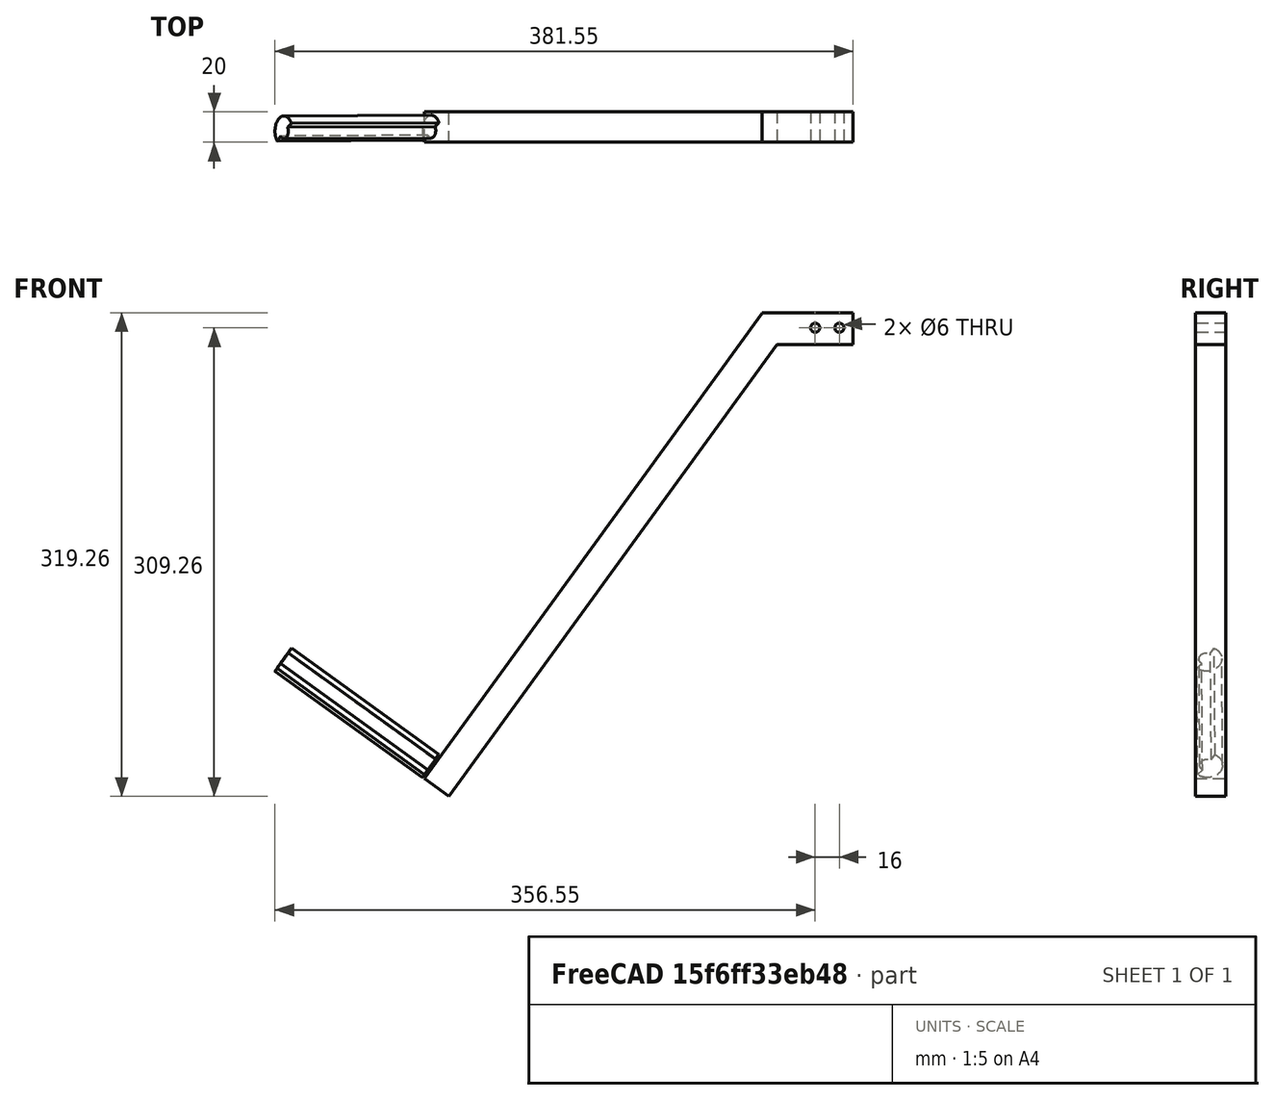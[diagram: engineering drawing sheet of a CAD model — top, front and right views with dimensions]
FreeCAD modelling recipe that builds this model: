
FCSTD DOCUMENT  (FreeCAD 0.16R6704 (Git))
Label: soporte reposapies derecho
License: All rights reserved
LicenseURL: http://en.wikipedia.org/wiki/All_rights_reserved
objects: Part::Cylinder×7, Part::Cut×6, Part::Box×2, Part::MultiFuse×2
note: 17 computed .brp shape members not serialized (recipe doc carries the construction recipe); baked Part::Feature solids carry a one-line shape summary decoded from their .brp

FEATURE [Part::Cylinder] Cylinder194  label="Agujero reposapies003"
  Angle = 360
  Height = 50
  Placement = pos=(-466,485,211) rot=(1,0,0;1.5708rad)
  Radius = 3
FEATURE [Part::Box] Box127  label="Cubo090"
  Height = 380
  Length = 20
  Placement = pos=(-291,469,-86.5) rot=(0,1,0;0.628319rad)
  Width = 20
FEATURE [Part::Box] Box128  label="Cubo091"
  Height = 21
  Length = 60
  Placement = pos=(-68,469,200) rot=(0,0,1;0rad)
  Width = 20
FEATURE [Part::MultiFuse] Fusion077
  Placement = pos=(15,0,0) rot=(0,0,1;0rad)
  Shapes = -> [Box127,Box128]
FEATURE [Part::Cylinder] Cylinder264  label="Cilindro154"
  Angle = 360
  Height = 37
  Placement = pos=(-2,496,211) rot=(1,0,0;1.5708rad)
  Radius = 3
FEATURE [Part::Cut] Cut283
  Base = -> Fusion077
  Placement = pos=(-448,-19,0) rot=(0,0,1;0rad)
  Tool = -> Cylinder264
FEATURE [Part::Cut] Cut286
  Base = -> Cut283
  Tool = -> Cylinder194
FEATURE [Part::Cylinder] Cylinder268  label="Cilindro155"
  Angle = 360
  Height = 120
  Placement = pos=(-292,0,98.9) rot=(0,1,0;2.19911rad)
  Radius = 10
FEATURE [Part::Cylinder] Cylinder269  label="Cilindro156"
  Angle = 50
  Height = 130
  Placement = pos=(-292,0,98.9) rot=(0,1,0;2.19911rad)
  Radius = 11
FEATURE [Part::Cylinder] Cylinder270  label="Cilindro157"
  Angle = 360
  Height = 130
  Placement = pos=(-292,0,98.9) rot=(0,1,0;2.19911rad)
  Radius = 5
FEATURE [Part::Cut] Cut289
  Base = -> Cylinder269
  Tool = -> Cylinder270
FEATURE [Part::Cylinder] Cylinder271  label="Cilindro158"
  Angle = 220
  Height = 120
  Placement = pos=(-292,0,98.9) rot=(0,1,0;2.19911rad)
  Radius = 11
FEATURE [Part::Cylinder] Cylinder272  label="Cilindro159"
  Angle = 360
  Height = 130
  Placement = pos=(-292,0,98.9) rot=(0,1,0;2.19911rad)
  Radius = 5
FEATURE [Part::Cut] Cut290
  Base = -> Cylinder271
  Tool = -> Cylinder272
FEATURE [Part::Cut] Cut291
  Base = -> Cut290
  Tool = -> Cut289
FEATURE [Part::Cut] Cut292
  Base = -> Cylinder268
  Placement = pos=(-905.244,441.276,167.725) rot=(0.584418,-0.083493,0.807146;3.14626rad)
  Tool = -> Cut291
FEATURE [Part::MultiFuse] Fusion083  label="Fusion085"
  Shapes = -> [Cut292,Cut286]
